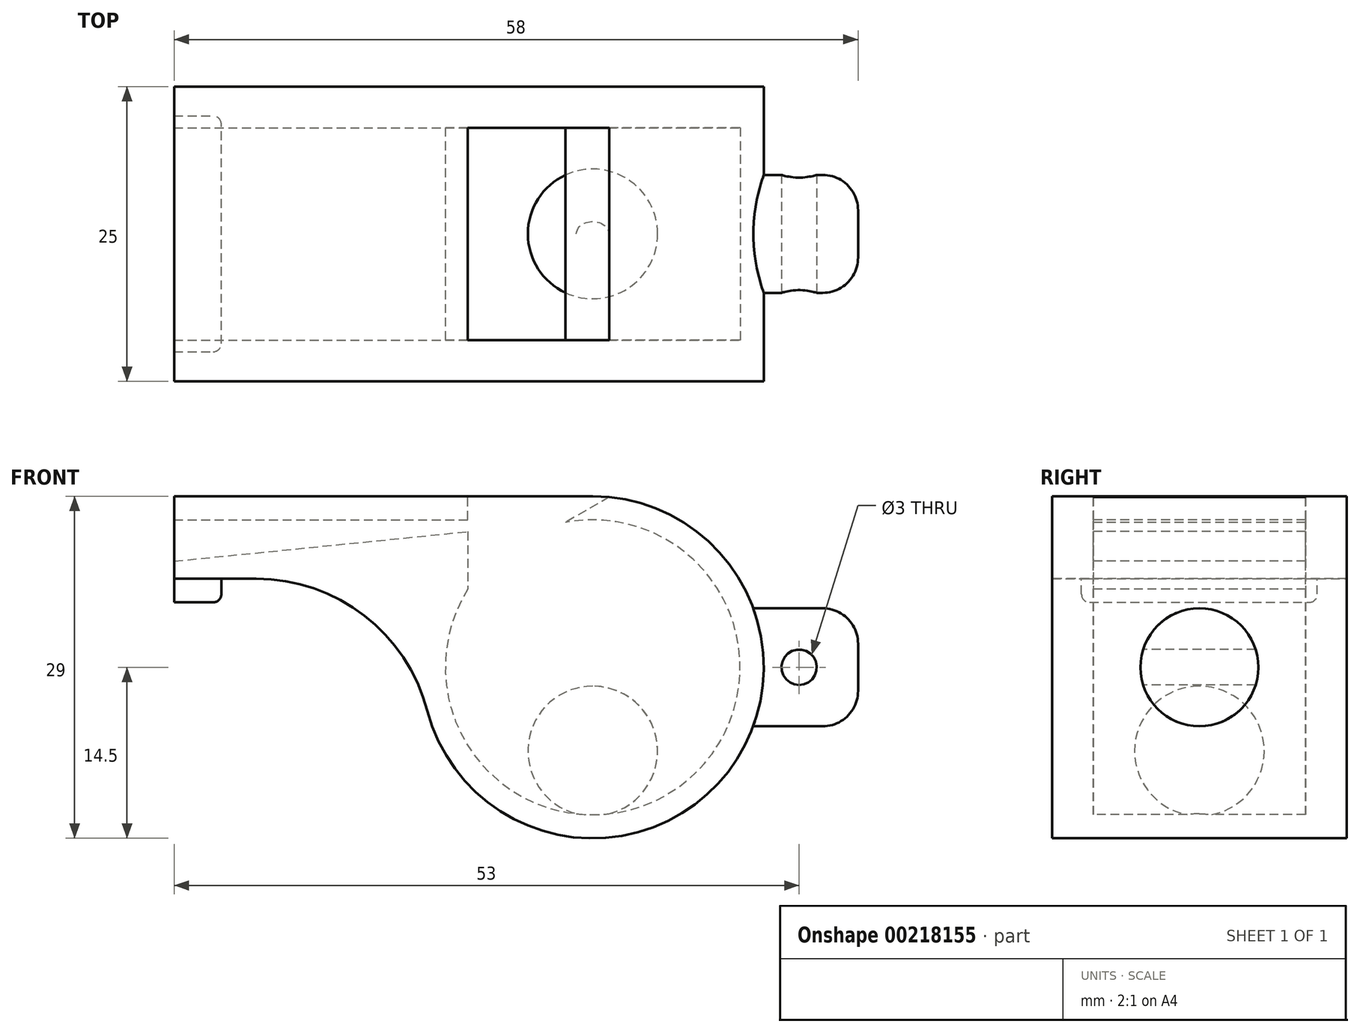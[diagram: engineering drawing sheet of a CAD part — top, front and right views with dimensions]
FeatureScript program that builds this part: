
annotation { "Feature Type Name" : "Feature", "Feature Type Description" : "" }
export const myFeature = defineFeature(function(context is Context, id is Id, definition is map)
    precondition{}
    {
        {
            var Q0;
            Q0=qCreatedBy(makeId("Front.planeOp"),FACE);
            var sketch = newSketch(context, id + "F0", { "sketchPlane" : qUnion([Q0])});
            skArc(sketch, "E0", {"start": v(-12.4, 7.5) * mm, "mid": v(7.12, -12.63) * mm, "end": v(0, 14.5) * mm});
            skLineSegment(sketch, "E1", {"start": v(0, 14.5) * mm, "end": v(-35.5, 14.5) * mm});
            skLineSegment(sketch, "E2", {"start": v(-35.5, 14.5) * mm, "end": v(-35.5, 7.5) * mm});
            skLineSegment(sketch, "E3", {"start": v(-35.5, 7.5) * mm, "end": v(-12.4, 7.5) * mm});
            skSolve(sketch);
        }
        {
            var Q0;
            Q0=makeQuery(id+"F0.imprint","IMPRINT",FACE,{"disambiguationData":[TD([[makeQuery(id+"F0.imprint","IMPRINT",EDGE,{"derivedFrom":sQuery(id+"F0.wireOp",EDGE,"E0")}),1.0]])]});
            extrude(context, id + "F1", {"entities" : qUnion([Q0]), "depth" : 25 * mm, "offsetDistance" : 25 * mm, "symmetric" : true});
        }
        {
            var Q0;
            Q0=qCreatedBy(makeId("Front.planeOp"),FACE);
            var sketch = newSketch(context, id + "F2", { "sketchPlane" : qUnion([Q0])});
            skArc(sketch, "E4", {"start": v(-10.59, 6.64) * mm, "mid": v(7.04, -10.33) * mm, "end": v(-2.3, 12.29) * mm});
            skLineSegment(sketch, "E5", {"start": v(-35.5, 12.5) * mm, "end": v(-35.5, 9) * mm});
            skLineSegment(sketch, "E6", {"start": v(-35.5, 9) * mm, "end": v(-10.59, 11.5) * mm});
            skLineSegment(sketch, "E7", {"start": v(-10.59, 11.5) * mm, "end": v(-10.59, 6.64) * mm});
            skLineSegment(sketch, "E8", {"start": v(-35.5, 12.5) * mm, "end": v(-10.59, 12.5) * mm});
            skLineSegment(sketch, "E9", {"start": v(-10.59, 12.5) * mm, "end": v(-10.59, 14.5) * mm});
            skLineSegment(sketch, "E10", {"start": v(-10.59, 14.5) * mm, "end": v(0, 14.5) * mm});
            skArc(sketch, "E11", {"start": v(0, 14.5) * mm, "mid": v(0.7, 14.48) * mm, "end": v(1.41, 14.43) * mm});
            skLineSegment(sketch, "E12", {"start": v(-35.5, 9) * mm, "end": v(3.58, 12.92) * mm, "construction": true});
            skLineSegment(sketch, "E13", {"start": v(1.41, 14.43) * mm, "end": v(-2.3, 12.29) * mm});
            skSolve(sketch);
        }
        {
            var Q0;
            Q0 = qSketchRegion(id + "F2", true);
            extrude(context, id + "F3", {"entities" : qUnion([Q0]), "operationType" : NewBodyOperationType.REMOVE, "oppositeDirection" : true, "depth" : 18 * mm, "offsetDistance" : 25 * mm, "symmetric" : true});
        }
        {
            var Q0;
            Q0=qCreatedBy(makeId("Front.planeOp"),FACE);
            var sketch = newSketch(context, id + "F4", { "sketchPlane" : qUnion([Q0])});
            skLineSegment(sketch, "E14.bottom", {"start": v(22.5, 0) * mm, "end": v(12.5, 0) * mm});
            skLineSegment(sketch, "E14.top", {"start": v(22.5, 5) * mm, "end": v(12.5, 5) * mm});
            skLineSegment(sketch, "E14.left", {"start": v(22.5, 0) * mm, "end": v(22.5, 5) * mm});
            skLineSegment(sketch, "E14.right", {"start": v(12.5, 0) * mm, "end": v(12.5, 5) * mm});
            skSolve(sketch);
        }
        {
            var Q0;
            Q0=makeQuery(id+"F4.imprint","IMPRINT",FACE,{"disambiguationData":[TD([[makeQuery(id+"F4.imprint","IMPRINT",EDGE,{"derivedFrom":sQuery(id+"F4.wireOp",EDGE,"E14.bottom")}),-1.0]])]});
            var Q1;
            Q1=sQuery(id+"F4.wireOp",EDGE,"E14.bottom");
            revolve(context, id + "F5", {"operationType" : NewBodyOperationType.ADD, "entities" : qUnion([Q0]), "axis" : qUnion([Q1]), "revolveType" : RevolveType.FULL});
        }
        {
            var Q0;
            Q0=makeQuery(id+"F5.opRevolve","SWEPT_EDGE",EDGE,{"disambiguationData":[OSD([sQuery(id+"F4.wireOp",EDGE,"E14.top"),sQuery(id+"F4.wireOp",EDGE,"E14.left")])]});
            fillet(context, id + "F6", {"entities" : qUnion([Q0]), "radius" : 3 * mm, "tangentPropagation" : true, "allowEdgeOverflow" : false});
        }
        {
            var Q0;
            Q0=qCreatedBy(makeId("Front.planeOp"),FACE);
            var sketch = newSketch(context, id + "F7", { "sketchPlane" : qUnion([Q0])});
            skCircle(sketch, "E15", {"center": v(17.5, 0) * mm, "radius": 1.5 * mm});
            skSolve(sketch);
        }
        {
            var Q0;
            Q0 = qSketchRegion(id + "F7", true);
            extrude(context, id + "F8", {"entities" : qUnion([Q0]), "operationType" : NewBodyOperationType.REMOVE, "endBound" : BoundingType.THROUGH_ALL, "oppositeDirection" : true, "depth" : 25 * mm, "offsetDistance" : 25 * mm, "hasSecondDirection" : true, "secondDirectionBound" : BoundingType.THROUGH_ALL, "secondDirectionOppositeDirection" : false, "secondDirectionDepth" : 25 * mm});
        }
        {
            var Q0;
            Q0=makeQuery(id+"F1.opExtrude","SWEPT_FACE",FACE,{"disambiguationData":[OSD([sQuery(id+"F0.wireOp",EDGE,"E3")])]});
            var sketch = newSketch(context, id + "F9", { "sketchPlane" : qUnion([Q0])});
            skLineSegment(sketch, "E16.bottom", {"start": v(-35.5, 10) * mm, "end": v(-31.5, 10) * mm});
            skLineSegment(sketch, "E16.top", {"start": v(-35.5, -10) * mm, "end": v(-31.5, -10) * mm});
            skLineSegment(sketch, "E16.left", {"start": v(-35.5, 10) * mm, "end": v(-35.5, -10) * mm});
            skLineSegment(sketch, "E16.right", {"start": v(-31.5, 10) * mm, "end": v(-31.5, -10) * mm});
            skSolve(sketch);
        }
        {
            var Q0;
            Q0 = qSketchRegion(id + "F9", true);
            extrude(context, id + "F10", {"entities" : qUnion([Q0]), "operationType" : NewBodyOperationType.ADD, "depth" : 2 * mm, "offsetDistance" : 25 * mm});
        }
        {
            var Q0;
            Q0=makeQuery(id+"F10.opExtrude","CAP_EDGE",EDGE,{"disambiguationData":[OSD([sQuery(id+"F9.wireOp",EDGE,"E16.bottom")])],"isStart":true});
            var Q1;
            Q1=makeQuery(id+"F10.opExtrude","CAP_EDGE",EDGE,{"disambiguationData":[OSD([sQuery(id+"F9.wireOp",EDGE,"E16.right")])],"isStart":true});
            var Q2;
            Q2=makeQuery(id+"F10.opExtrude","CAP_EDGE",EDGE,{"disambiguationData":[OSD([sQuery(id+"F9.wireOp",EDGE,"E16.top")])],"isStart":true});
            var Q3;
            Q3=makeQuery(id+"F10.opExtrude","CAP_EDGE",EDGE,{"disambiguationData":[OSD([sQuery(id+"F9.wireOp",EDGE,"E16.top")])],"isStart":false});
            var Q4;
            Q4=makeQuery(id+"F10.opExtrude","CAP_EDGE",EDGE,{"disambiguationData":[OSD([sQuery(id+"F9.wireOp",EDGE,"E16.right")])],"isStart":false});
            var Q5;
            Q5=makeQuery(id+"F10.opExtrude","CAP_EDGE",EDGE,{"disambiguationData":[OSD([sQuery(id+"F9.wireOp",EDGE,"E16.bottom")])],"isStart":false});
            var Q6;
            Q6=makeQuery(id+"F10.opExtrude","SWEPT_EDGE",EDGE,{"disambiguationData":[OSD([sQuery(id+"F9.wireOp",EDGE,"E16.top"),sQuery(id+"F9.wireOp",EDGE,"E16.right")])]});
            var Q7;
            Q7=makeQuery(id+"F10.opExtrude","SWEPT_EDGE",EDGE,{"disambiguationData":[OSD([sQuery(id+"F9.wireOp",EDGE,"E16.bottom"),sQuery(id+"F9.wireOp",EDGE,"E16.right")])]});
            fillet(context, id + "F11", {"entities" : qUnion([Q0, Q1, Q2, Q3, Q4, Q5, Q6, Q7]), "radius" : 0.7 * mm, "tangentPropagation" : true, "allowEdgeOverflow" : false});
        }
        {
            var Q0;
            Q0=makeQuery(id+"F1.opExtrude","SWEPT_EDGE",EDGE,{"disambiguationData":[OSD([sQuery(id+"F0.wireOp",EDGE,"E0"),sQuery(id+"F0.wireOp",EDGE,"E3")])]});
            fillet(context, id + "F12", {"entities" : qUnion([Q0]), "radius" : 15 * mm, "tangentPropagation" : true, "allowEdgeOverflow" : false});
        }
        {
            var Q0;
            Q0=qCreatedBy(makeId("Front.planeOp"),FACE);
            var sketch = newSketch(context, id + "F13", { "sketchPlane" : qUnion([Q0])});
            skArc(sketch, "E17", {"start": v(0, -1.6) * mm, "mid": v(-5.5, -7.1) * mm, "end": v(0, -12.6) * mm});
            skLineSegment(sketch, "E18", {"start": v(0, -1.6) * mm, "end": v(0, -12.6) * mm});
            skSolve(sketch);
        }
        {
            var Q0;
            Q0 = qSketchRegion(id + "F13", true);
            var Q1;
            Q1=sQuery(id+"F13.wireOp",EDGE,"E18");
            revolve(context, id + "F14", {"operationType" : NewBodyOperationType.ADD, "entities" : qUnion([Q0]), "axis" : qUnion([Q1]), "revolveType" : RevolveType.FULL});
        }
    });
